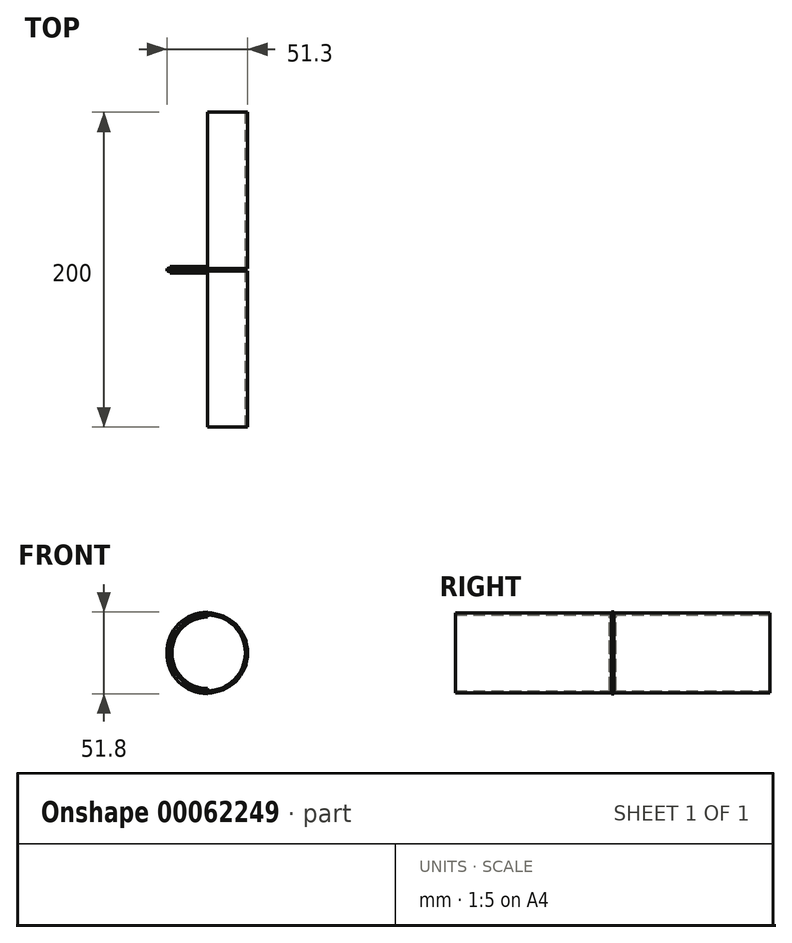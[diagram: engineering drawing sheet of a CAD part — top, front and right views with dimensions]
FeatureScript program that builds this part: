
annotation { "Feature Type Name" : "Feature", "Feature Type Description" : "" }
export const myFeature = defineFeature(function(context is Context, id is Id, definition is map)
    precondition{}
    {
        {
            var Q0;
            Q0=qCreatedBy(makeId("Front.planeOp"),FACE);
            var sketch = newSketch(context, id + "F0", { "sketchPlane" : qUnion([Q0])});
            skCircle(sketch, "E0", {"center": v(0, 0) * mm, "radius": 25.4 * mm});
            skCircle(sketch, "E1.0", {"center": v(0, 0) * mm, "radius": 24 * mm});
            skLineSegment(sketch, "E2", {"start": v(0, 30.7) * mm, "end": v(0, -32.6) * mm});
            skSolve(sketch);
        }
        {
            var Q0;
            {var subQ0=sQuery(id+"F0.wireOp",EDGE,"E2");var subQ3=sQuery(id+"F0.wireOp",EDGE,"E0");var subQ6=makeQuery(id+"F0.imprint","INTERSECT",VERTEX,{"disambiguationData":[OD(0.0)],"derivedFrom":[subQ3,subQ0]});Q0=makeQuery(id+"F0.imprint","IMPRINT",FACE,{"disambiguationData":[TD([[makeQuery(id+"F0.imprint","IMPRINT",EDGE,{"disambiguationData":[TD([[subQ6,-1.0]])],"derivedFrom":subQ3}),1.0]])]});}
            extrude(context, id + "F1", {"entities" : qUnion([Q0]), "endBound" : BoundingType.SYMMETRIC, "depth" : 200 * mm});
        }
        {
            var Q0;
            Q0=qCreatedBy(makeId("Front.planeOp"),FACE);
            var sketch = newSketch(context, id + "F2", { "sketchPlane" : qUnion([Q0])});
            skCircle(sketch, "E3.0", {"center": v(0, 0) * mm, "radius": 25.4 * mm});
            skSolve(sketch);
        }
        {
            var Q0;
            Q0=qSketchRegion(id+"F2",true);
            extrude(context, id + "F3", {"entities" : qUnion([Q0]), "operationType" : NewBodyOperationType.REMOVE, "endBound" : BoundingType.SYMMETRIC, "oppositeDirection" : true, "depth" : 1.5 * mm});
        }
        {
            var Q0;
            Q0=qCreatedBy(makeId("Right.planeOp"),FACE);
            var sketch = newSketch(context, id + "F4", { "sketchPlane" : qUnion([Q0])});
            skLineSegment(sketch, "E4.0", {"start": v(-0.75, 25.9) * mm, "end": v(-0.75, 24) * mm});
            skLineSegment(sketch, "E4.1", {"start": v(0.75, 25.9) * mm, "end": v(0.75, 24) * mm});
            skPoint(sketch, "E5.orphan", {"position": v(-0.75, 25.4) * mm});
            skPoint(sketch, "E6.orphan", {"position": v(0.75, 25.4) * mm});
            skLineSegment(sketch, "E7", {"start": v(-0.75, 25.9) * mm, "end": v(0.75, 25.9) * mm});
            skLineSegment(sketch, "E8", {"start": v(-2, 23.7) * mm, "end": v(-2, 22.7) * mm});
            skLineSegment(sketch, "E9", {"start": v(-2, 22.7) * mm, "end": v(2, 22.7) * mm});
            skLineSegment(sketch, "E10.MirrorCS", {"start": v(2, 23.7) * mm, "end": v(2, 22.7) * mm});
            skLineSegment(sketch, "E11.0", {"start": v(-1.48, 24) * mm, "end": v(-0.75, 24) * mm});
            skLineSegment(sketch, "E11.1", {"start": v(0.75, 24) * mm, "end": v(1.48, 24) * mm});
            skPoint(sketch, "E12.orphan", {"position": v(-100, 24) * mm});
            skPoint(sketch, "E13.orphan", {"position": v(100, 24) * mm});
            skLineSegment(sketch, "E14", {"start": v(-2, 23.7) * mm, "end": v(-1.48, 24) * mm});
            skLineSegment(sketch, "E15.MirrorCS", {"start": v(2, 23.7) * mm, "end": v(1.48, 24) * mm});
            skLineSegment(sketch, "E16", {"start": v(0, 0) * mm, "end": v(15.22, 0) * mm, "construction": true});
            skLineSegment(sketch, "E17.0", {"start": v(0.75, 25.4) * mm, "end": v(100, 25.4) * mm});
            skSolve(sketch);
        }
        {
            var Q0;
            {var subQ3=sQuery(id+"F4.wireOp",EDGE,"E4.0");Q0=makeQuery(id+"F4.imprint","IMPRINT",FACE,{"disambiguationData":[TD([[makeQuery(id+"F4.imprint","IMPRINT",EDGE,{"derivedFrom":subQ3}),1.0]])]});}
            var Q1;
            {var subQ0=sQuery(id+"F0.wireOp",EDGE,"E1.0");Q1=makeQuery(id+"F3.boolean.opBoolean","SPLIT",FACE,{"disambiguationData":[TD([makeQuery(id+"F3.opExtrude","CAP_FACE",FACE,{"disambiguationData":[OSD([sQuery(id+"F2.wireOp",EDGE,"E3.0")])],"isStart":false})])],"derivedFrom":makeQuery(id+"F1.opExtrude","SWEPT_FACE",FACE,{"disambiguationData":[OSD([subQ0])]})});}
            revolve(context, id + "F5", {"entities" : qUnion([Q0]), "axis" : qUnion([Q1]), "revolveType" : RevolveType.ONE_DIRECTION, "angle" : 180 * degree});
        }
    });
